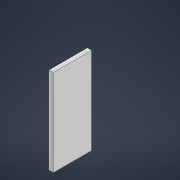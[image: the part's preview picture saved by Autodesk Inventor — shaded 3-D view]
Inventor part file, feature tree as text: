
AUTODESK INVENTOR PART (.ipt)
format: ipt  version: 2022 (Build 260153000, 153)  size: 87,040 bytes
history: native  units: mm
features: other x1, sketch x1, extrude x1
ambient origin geometry x8: Origin, YZ Plane, XZ Plane, XY Plane, X Axis, Y Axis, Z Axis, Center Point
bodies: Body1 (feature_tree)
feature tree (3):
  other  "Твердое тело1"
  sketch  "Эскиз1"
  extrude  "Выдавливание1"  Depth=266.0mm
